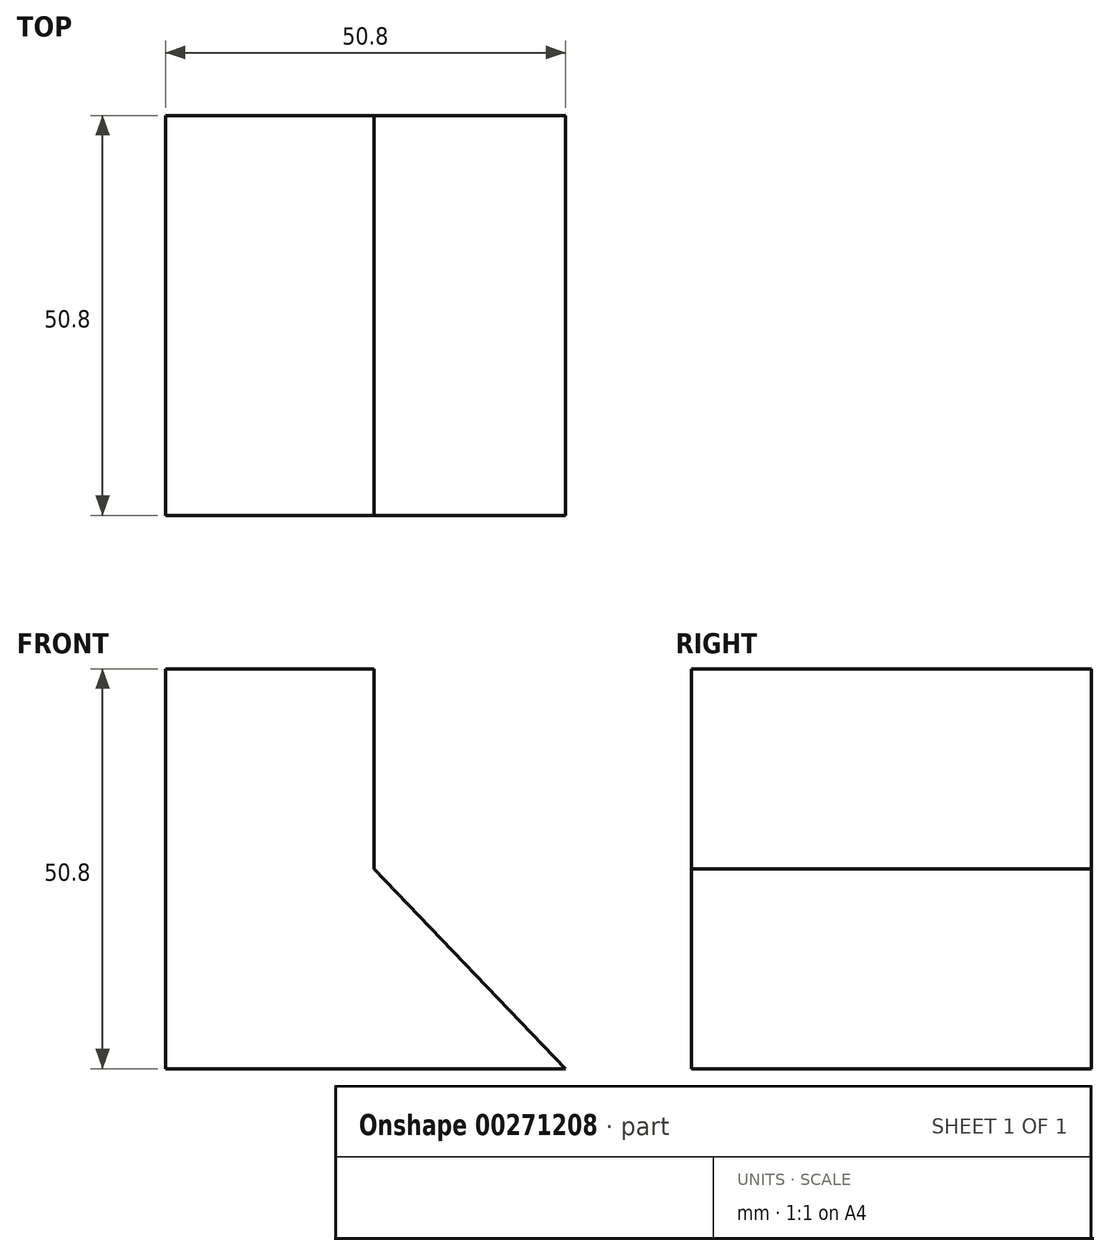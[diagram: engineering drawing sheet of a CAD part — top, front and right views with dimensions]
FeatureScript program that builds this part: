
annotation { "Feature Type Name" : "Feature", "Feature Type Description" : "" }
export const myFeature = defineFeature(function(context is Context, id is Id, definition is map)
    precondition{}
    {
        {
            var Q0;
            Q0=qCreatedBy(makeId("Front.planeOp"),FACE);
            var sketch = newSketch(context, id + "F0", { "sketchPlane" : qUnion([Q0])});
            skLineSegment(sketch, "E0.bottom", {"start": v(0, 0) * mm, "end": v(-50.8, 0) * mm});
            skLineSegment(sketch, "E0.top", {"start": v(0, 50.8) * mm, "end": v(-50.8, 50.8) * mm});
            skLineSegment(sketch, "E0.left", {"start": v(0, 0) * mm, "end": v(0, 50.8) * mm});
            skLineSegment(sketch, "E0.right", {"start": v(-50.8, 0) * mm, "end": v(-50.8, 50.8) * mm});
            skSolve(sketch);
        }
        {
            var Q0;
            Q0 = qSketchRegion(id + "F0", true);
            extrude(context, id + "F1", {"entities" : qUnion([Q0]), "depth" : 50.8 * mm});
        }
        {
            var Q0;
            Q0=makeQuery(id+"F1.opExtrude","CAP_FACE",FACE,{"disambiguationData":[OSD([sQuery(id+"F0.wireOp",EDGE,"E0.bottom"),sQuery(id+"F0.wireOp",EDGE,"E0.top"),sQuery(id+"F0.wireOp",EDGE,"E0.left"),sQuery(id+"F0.wireOp",EDGE,"E0.right")])],"isStart":false});
            var sketch = newSketch(context, id + "F2", { "sketchPlane" : qUnion([Q0])});
            skLineSegment(sketch, "E1", {"start": v(0, 0) * mm, "end": v(-24.3, 25.4) * mm});
            skPoint(sketch, "E1.endSnap0", {"position": v(0, 25.4) * mm});
            skLineSegment(sketch, "E2", {"start": v(-24.3, 25.4) * mm, "end": v(-24.3, 50.8) * mm});
            skLineSegment(sketch, "E3", {"start": v(-24.3, 50.8) * mm, "end": v(0, 50.8) * mm});
            skLineSegment(sketch, "E4", {"start": v(0, 50.8) * mm, "end": v(0, 0) * mm});
            skSolve(sketch);
        }
        {
            var Q0;
            Q0 = qSketchRegion(id + "F2", true);
            extrude(context, id + "F3", {"entities" : qUnion([Q0]), "operationType" : NewBodyOperationType.REMOVE, "oppositeDirection" : true, "depth" : 50.8 * mm});
        }
    });
